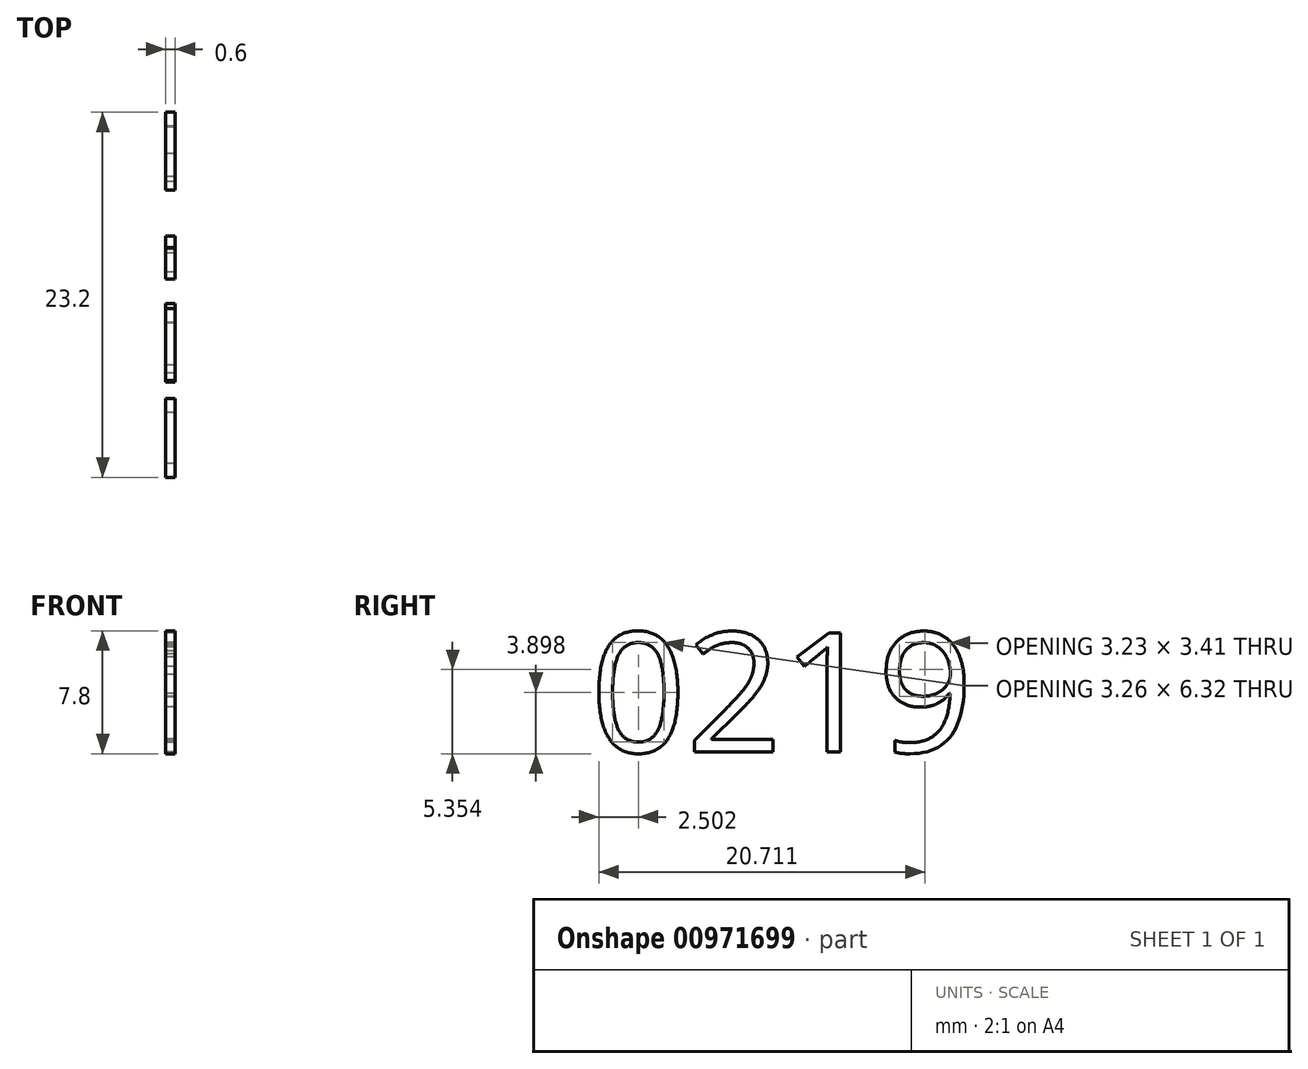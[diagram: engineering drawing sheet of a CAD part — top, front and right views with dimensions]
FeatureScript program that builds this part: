
annotation { "Feature Type Name" : "Feature", "Feature Type Description" : "" }
export const myFeature = defineFeature(function(context is Context, id is Id, definition is map)
    precondition{}
    {
        {
            var Q0;
            Q0=qCreatedBy(makeId("Right.planeOp"),FACE);
            var sketch = newSketch(context, id + "F0", { "sketchPlane" : qUnion([Q0])});
            skText(sketch, "E0", { "text": "0219\n", "fontName": "OpenSans-Regular.ttf"});
            const initialGuessF0  = {"E0": [-0.01465, 0.00457, 1, 0, 0.00765]};
            skSetInitialGuess(sketch, initialGuessF0);
            skSolve(sketch);
        }
        {
            var Q0;
            Q0=makeQuery(id+"F0.imprint","IMPRINT",FACE,{"disambiguationData":[TD([[makeQuery(id+"F0.imprint","IMPRINT",EDGE,{"derivedFrom":sQuery(id+"F0.wireOp",EDGE,"E0.sketch_text.stroke-0")}),-1.0]])]});
            var Q1;
            Q1=makeQuery(id+"F0.imprint","IMPRINT",FACE,{"disambiguationData":[TD([[makeQuery(id+"F0.imprint","IMPRINT",EDGE,{"derivedFrom":sQuery(id+"F0.wireOp",EDGE,"E0.sketch_text.stroke-16")}),-1.0]])]});
            var Q2;
            Q2=makeQuery(id+"F0.imprint","IMPRINT",FACE,{"disambiguationData":[TD([[makeQuery(id+"F0.imprint","IMPRINT",EDGE,{"derivedFrom":sQuery(id+"F0.wireOp",EDGE,"E0.sketch_text.stroke-36")}),-1.0]])]});
            var Q3;
            Q3=makeQuery(id+"F0.imprint","IMPRINT",FACE,{"disambiguationData":[TD([[makeQuery(id+"F0.imprint","IMPRINT",EDGE,{"derivedFrom":sQuery(id+"F0.wireOp",EDGE,"E0.sketch_text.stroke-45")}),-1.0]])]});
            extrude(context, id + "F1", {"entities" : qUnion([Q0, Q1, Q2, Q3]), "depth" : .6 * mm, "offsetDistance" : 25 * mm});
        }
    });
